# Revit family: Quad solo
name_source: partatom
category: Lighting Fixtures
units: mm (PartAtom-declared; Revit-internal decimal feet)

## family parameters
Always vertical = Yes
Cut with Voids When Loaded = No
Host = Ceiling
Light Source = Yes
OmniClass Number = 23.80.70.11
OmniClass Title = Luminaries for Internal Lighting
Part Type = Normal
Room Calculation Point = No
Round Connector Dimension = Use Diameter
Shared = No

## types (3) — shared parameters
Color Filter = 16777215
Dimming Lamp Color Temperature Shift = <None>
Emit Shape Visible in Rendering = No
Emit from Rectangle Length = 48 "
Emit from Rectangle Width = 24 "
L = 3.87 "
Photometric Web File = generic
Tilt Angle = 60.00°

## type names
- Quad solo drywall
- Quad solo center of tile
- Quad solo tgrid
type visibility flags: 3 boolean params named "<type name> ON" — each type sets only its own to Yes (folded from table)

## geometry (parser evidence)
native form markers: Sweep x11
no freeform markers — native parametric forms only
